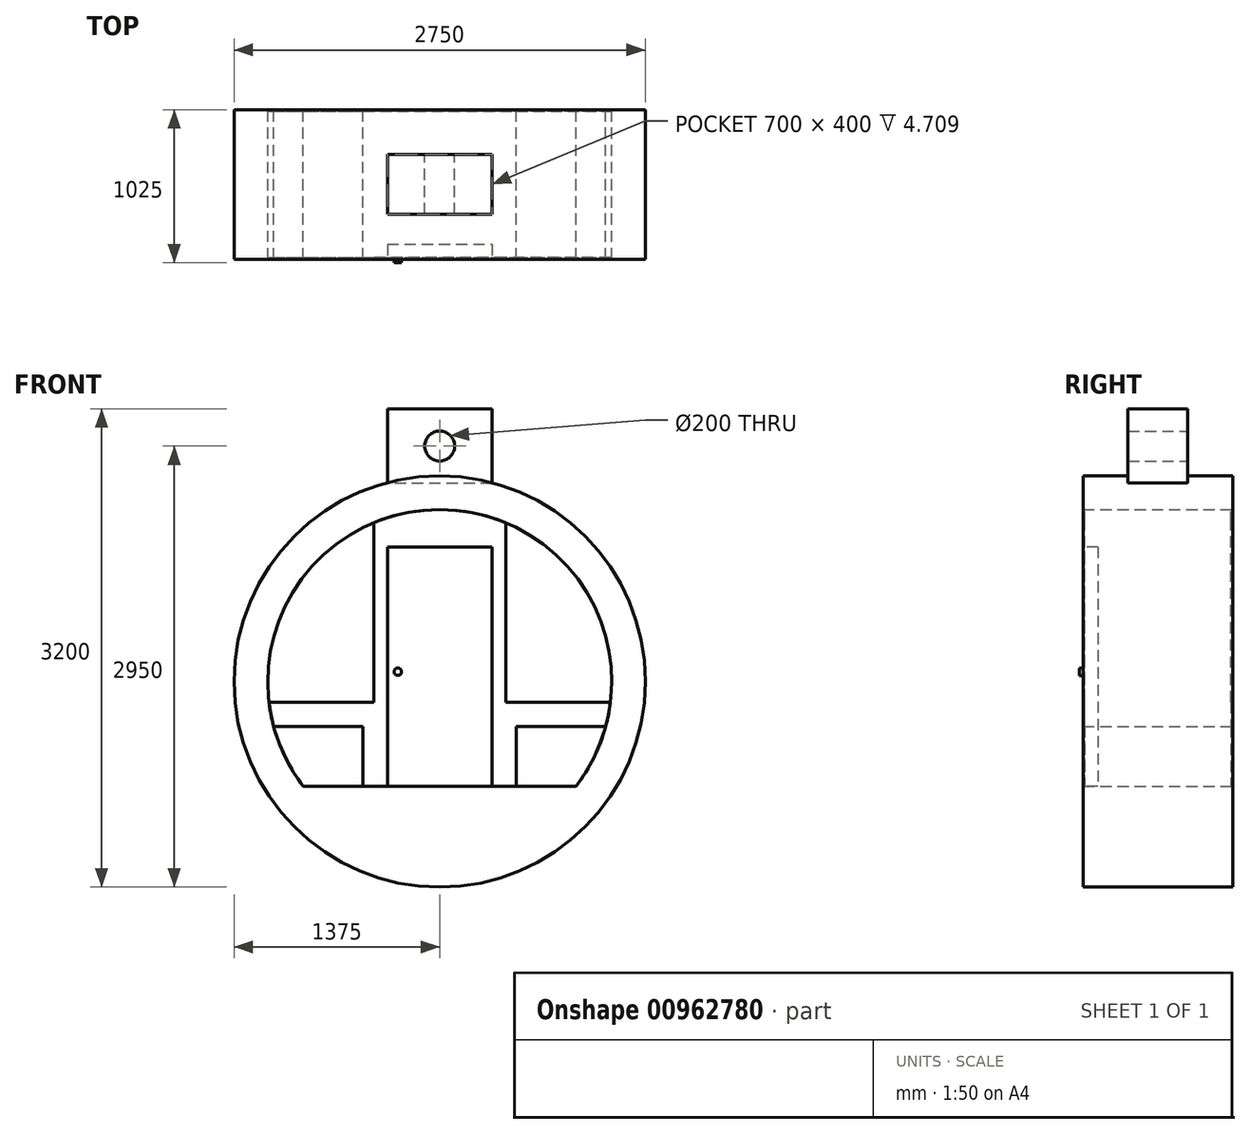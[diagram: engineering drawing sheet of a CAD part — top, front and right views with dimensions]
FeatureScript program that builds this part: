
annotation { "Feature Type Name" : "Feature", "Feature Type Description" : "" }
export const myFeature = defineFeature(function(context is Context, id is Id, definition is map)
    precondition{}
    {
        {
            var Q0;
            Q0=qCreatedBy(makeId("Front.planeOp"),FACE);
            var sketch = newSketch(context, id + "F0", { "sketchPlane" : qUnion([Q0])});
            skLineSegment(sketch, "E0.bottom", {"start": v(350, 3250) * mm, "end": v(-350, 3250) * mm});
            skLineSegment(sketch, "E0.top", {"start": v(350, 2750) * mm, "end": v(-350, 2750) * mm});
            skLineSegment(sketch, "E0.left", {"start": v(350, 3250) * mm, "end": v(350, 2750) * mm});
            skLineSegment(sketch, "E0.right", {"start": v(-350, 3250) * mm, "end": v(-350, 2750) * mm});
            skPoint(sketch, "E0.middle", {"position": v(0, 3000) * mm});
            skCircle(sketch, "E1", {"center": v(0, 3000) * mm, "radius": 100 * mm});
            skSolve(sketch);
        }
        {
            var Q0;
            Q0=qSketchRegion(id+"F0",true);
            extrude(context, id + "F1", {"entities" : qUnion([Q0]), "endBound" : BoundingType.SYMMETRIC, "depth" : 400 * mm, "offsetDistance" : 25 * mm});
        }
        {
            var Q0;
            Q0=qCreatedBy(makeId("Front.planeOp"),FACE);
            var sketch = newSketch(context, id + "F2", { "sketchPlane" : qUnion([Q0])});
            skLineSegment(sketch, "E2", {"start": v(0, 0) * mm, "end": v(0, 2750) * mm, "construction": true});
            skPoint(sketch, "E3", {"position": v(0, 1375) * mm});
            skCircle(sketch, "E4", {"center": v(0, 1375) * mm, "radius": 1375 * mm});
            skCircle(sketch, "E5", {"center": v(0, 1375) * mm, "radius": 1150 * mm});
            skLineSegment(sketch, "E6", {"start": v(-912.41, 675) * mm, "end": v(912.41, 675) * mm});
            skSolve(sketch);
        }
        {
            var Q0;
            Q0=qSketchRegion(id+"F2",true);
            var Q1;
            {var subQ0=sQuery(id+"F2.wireOp",EDGE,"E6");Q1=makeQuery(id+"F2.imprint","IMPRINT",FACE,{"disambiguationData":[TD([[makeQuery(id+"F2.imprint","IMPRINT",EDGE,{"derivedFrom":subQ0}),-1.0]])]});}
            extrude(context, id + "F3", {"entities" : qUnion([Q0, Q1]), "operationType" : NewBodyOperationType.ADD, "endBound" : BoundingType.SYMMETRIC, "depth" : 1000 * mm, "offsetDistance" : 25 * mm});
        }
        {
            var Q0;
            Q0=qCreatedBy(makeId("Front.planeOp"),FACE);
            var sketch = newSketch(context, id + "F4", { "sketchPlane" : qUnion([Q0])});
            skLineSegment(sketch, "E7", {"start": v(512.41, 675) * mm, "end": v(512.41, 1075) * mm});
            skLineSegment(sketch, "E8", {"start": v(512.41, 1075) * mm, "end": v(1110.18, 1075) * mm});
            skLineSegment(sketch, "E9.MirrorCS", {"start": v(-512.41, 675) * mm, "end": v(-512.41, 1075) * mm});
            skLineSegment(sketch, "E10.MirrorCS", {"start": v(-512.41, 1075) * mm, "end": v(-1110.18, 1075) * mm});
            skLineSegment(sketch, "E11", {"start": v(512.41, 675) * mm, "end": v(912.41, 675) * mm});
            skArc(sketch, "E12", {"start": v(912.41, 675) * mm, "mid": v(1030.88, 865.32) * mm, "end": v(1110.18, 1075) * mm});
            skArc(sketch, "E13.MirrorCS", {"start": v(-912.41, 675) * mm, "mid": v(-1030.88, 865.32) * mm, "end": v(-1110.18, 1075) * mm});
            skLineSegment(sketch, "E14.MirrorCS", {"start": v(-512.41, 675) * mm, "end": v(-912.41, 675) * mm});
            skSolve(sketch);
        }
        {
            var Q0;
            Q0=qSketchRegion(id+"F4",true);
            extrude(context, id + "F5", {"entities" : qUnion([Q0]), "endBound" : BoundingType.SYMMETRIC, "depth" : 1000 * mm, "offsetDistance" : 25 * mm});
        }
        {
            var Q0;
            Q0=makeQuery(id+"F3.opExtrude","CAP_FACE",FACE,{"disambiguationData":[OSD([sQuery(id+"F2.wireOp",EDGE,"E4"),sQuery(id+"F2.wireOp",EDGE,"E5"),sQuery(id+"F2.wireOp",EDGE,"E6")])],"isStart":false});
            var sketch = newSketch(context, id + "F6", { "sketchPlane" : qUnion([Q0])});
            skLineSegment(sketch, "E15", {"start": v(-350, 2275) * mm, "end": v(350, 2275) * mm});
            skLineSegment(sketch, "E16", {"start": v(350, 2275) * mm, "end": v(350, 675) * mm});
            skLineSegment(sketch, "E17", {"start": v(350, 675) * mm, "end": v(-350, 675) * mm});
            skLineSegment(sketch, "E18", {"start": v(-350, 675) * mm, "end": v(-350, 2275) * mm});
            skPoint(sketch, "E19", {"position": v(0, 675) * mm});
            skSolve(sketch);
        }
        {
            var Q0;
            Q0=qSketchRegion(id+"F6",true);
            extrude(context, id + "F7", {"entities" : qUnion([Q0]), "oppositeDirection" : true, "depth" : 100 * mm, "offsetDistance" : 25 * mm});
        }
        {
            var Q0;
            Q0=makeQuery(id+"F7.opExtrude","CAP_FACE",FACE,{"disambiguationData":[OSD([sQuery(id+"F6.wireOp",EDGE,"E15"),sQuery(id+"F6.wireOp",EDGE,"E16"),sQuery(id+"F6.wireOp",EDGE,"E17"),sQuery(id+"F6.wireOp",EDGE,"E18")])],"isStart":true});
            var sketch = newSketch(context, id + "F8", { "sketchPlane" : qUnion([Q0])});
            skCircle(sketch, "E20", {"center": v(-280, 1440.53) * mm, "radius": 25 * mm});
            skSolve(sketch);
        }
        {
            var Q0;
            Q0=qSketchRegion(id+"F8",true);
            extrude(context, id + "F9", {"entities" : qUnion([Q0]), "depth" : 25 * mm, "offsetDistance" : 25 * mm});
        }
        {
            var Q0;
            Q0=makeQuery(id+"F7.opExtrude","CAP_FACE",FACE,{"disambiguationData":[OSD([sQuery(id+"F6.wireOp",EDGE,"E15"),sQuery(id+"F6.wireOp",EDGE,"E16"),sQuery(id+"F6.wireOp",EDGE,"E17"),sQuery(id+"F6.wireOp",EDGE,"E18")])],"isStart":true});
            var sketch = newSketch(context, id + "F10", { "sketchPlane" : qUnion([Q0])});
            skLineSegment(sketch, "E21", {"start": v(-1141.67, 1236.8) * mm, "end": v(-441.67, 1236.8) * mm});
            skLineSegment(sketch, "E22", {"start": v(-441.67, 1236.8) * mm, "end": v(-441.67, 2436.8) * mm});
            skArc(sketch, "E23", {"start": v(-441.67, 2436.8) * mm, "mid": v(0, 2525) * mm, "end": v(441.67, 2436.8) * mm});
            skArc(sketch, "E24", {"start": v(-1141.67, 1236.8) * mm, "mid": v(-1128.83, 1155.34) * mm, "end": v(-1110.18, 1075) * mm});
            skLineSegment(sketch, "E25.MirrorCS", {"start": v(441.67, 1236.8) * mm, "end": v(441.67, 2436.8) * mm});
            skLineSegment(sketch, "E26.MirrorCS", {"start": v(1141.67, 1236.8) * mm, "end": v(441.67, 1236.8) * mm});
            skArc(sketch, "E27.MirrorCS", {"start": v(1141.67, 1236.8) * mm, "mid": v(1128.83, 1155.34) * mm, "end": v(1110.18, 1075) * mm});
            skLineSegment(sketch, "E28", {"start": v(-1110.18, 1075) * mm, "end": v(-512.41, 1075) * mm});
            skLineSegment(sketch, "E29", {"start": v(-512.41, 1075) * mm, "end": v(-512.41, 675) * mm});
            skLineSegment(sketch, "E30", {"start": v(-512.41, 675) * mm, "end": v(-350, 675) * mm});
            skLineSegment(sketch, "E31", {"start": v(-350, 675) * mm, "end": v(-350, 2275) * mm});
            skLineSegment(sketch, "E32", {"start": v(-350, 2275) * mm, "end": v(350, 2275) * mm});
            skLineSegment(sketch, "E33", {"start": v(350, 2275) * mm, "end": v(350, 675) * mm});
            skLineSegment(sketch, "E34", {"start": v(350, 675) * mm, "end": v(512.41, 675) * mm});
            skLineSegment(sketch, "E35", {"start": v(512.41, 675) * mm, "end": v(512.41, 1075) * mm});
            skLineSegment(sketch, "E36", {"start": v(512.41, 1075) * mm, "end": v(1110.18, 1075) * mm});
            skSolve(sketch);
        }
        {
            var Q0;
            Q0=qSketchRegion(id+"F10",true);
            extrude(context, id + "F11", {"entities" : qUnion([Q0]), "oppositeDirection" : true, "depth" : 10 * mm, "offsetDistance" : 25 * mm});
        }
        {
            var Q0;
            Q0=makeQuery(id+"F11.opExtrude","SWEPT_BODY",BODY,{"disambiguationData":[OSD([sQuery(id+"F10.wireOp",EDGE,"E21"),sQuery(id+"F10.wireOp",EDGE,"E22"),sQuery(id+"F10.wireOp",EDGE,"E23"),sQuery(id+"F10.wireOp",EDGE,"E24"),sQuery(id+"F10.wireOp",EDGE,"E25.MirrorCS"),sQuery(id+"F10.wireOp",EDGE,"E26.MirrorCS"),sQuery(id+"F10.wireOp",EDGE,"E27.MirrorCS"),sQuery(id+"F10.wireOp",EDGE,"E28"),sQuery(id+"F10.wireOp",EDGE,"E29"),sQuery(id+"F10.wireOp",EDGE,"E30"),sQuery(id+"F10.wireOp",EDGE,"E31"),sQuery(id+"F10.wireOp",EDGE,"E32"),sQuery(id+"F10.wireOp",EDGE,"E33"),sQuery(id+"F10.wireOp",EDGE,"E34"),sQuery(id+"F10.wireOp",EDGE,"E35"),sQuery(id+"F10.wireOp",EDGE,"E36")])]});
            var Q1;
            Q1=qCreatedBy(makeId("Front.planeOp"),FACE);
            mirror(context, id + "F12", {"entities" : qUnion([Q0]), "mirrorPlane" : qUnion([Q1])});
        }
        {
            var Q0;
            Q0=makeQuery(id+"F12.opPattern","COPY",FACE,{"derivedFrom":makeQuery(id+"F11.opExtrude","CAP_FACE",FACE,{"disambiguationData":[OSD([sQuery(id+"F10.wireOp",EDGE,"E21"),sQuery(id+"F10.wireOp",EDGE,"E22"),sQuery(id+"F10.wireOp",EDGE,"E23"),sQuery(id+"F10.wireOp",EDGE,"E24"),sQuery(id+"F10.wireOp",EDGE,"E25.MirrorCS"),sQuery(id+"F10.wireOp",EDGE,"E26.MirrorCS"),sQuery(id+"F10.wireOp",EDGE,"E27.MirrorCS"),sQuery(id+"F10.wireOp",EDGE,"E28"),sQuery(id+"F10.wireOp",EDGE,"E29"),sQuery(id+"F10.wireOp",EDGE,"E30"),sQuery(id+"F10.wireOp",EDGE,"E31"),sQuery(id+"F10.wireOp",EDGE,"E32"),sQuery(id+"F10.wireOp",EDGE,"E33"),sQuery(id+"F10.wireOp",EDGE,"E34"),sQuery(id+"F10.wireOp",EDGE,"E35"),sQuery(id+"F10.wireOp",EDGE,"E36")])],"isStart":true}),"instanceName":"1"});
            var sketch = newSketch(context, id + "F13", { "sketchPlane" : qUnion([Q0])});
            skLineSegment(sketch, "E37.bottom", {"start": v(-350, 2275) * mm, "end": v(350, 2275) * mm});
            skLineSegment(sketch, "E37.top", {"start": v(-350, 675) * mm, "end": v(350, 675) * mm});
            skLineSegment(sketch, "E37.left", {"start": v(-350, 2275) * mm, "end": v(-350, 675) * mm});
            skLineSegment(sketch, "E37.right", {"start": v(350, 2275) * mm, "end": v(350, 675) * mm});
            skSolve(sketch);
        }
        {
            var Q0;
            Q0=qSketchRegion(id+"F13",true);
            extrude(context, id + "F14", {"entities" : qUnion([Q0]), "operationType" : NewBodyOperationType.ADD, "oppositeDirection" : true, "depth" : 10 * mm, "offsetDistance" : 25 * mm});
        }
        {
            var Q0;
            Q0=makeQuery(id+"F1.opExtrude","SWEPT_BODY",BODY,{"disambiguationData":[OSD([sQuery(id+"F0.wireOp",EDGE,"E0.bottom"),sQuery(id+"F0.wireOp",EDGE,"E0.top"),sQuery(id+"F0.wireOp",EDGE,"E0.left"),sQuery(id+"F0.wireOp",EDGE,"E0.right"),sQuery(id+"F0.wireOp",EDGE,"E1")])]});
            transform(context, id + "F15", {"entities" : qUnion([Q0]), "transformType" : TransformType.TRANSLATION_3D, "dx" : 0 * mm, "dy" : 0 * mm, "dz" : -50 * mm, "makeCopy" : false});
        }
        {
            var Q0;
            Q0=makeQuery(id+"F1.opExtrude","SWEPT_BODY",BODY,{"disambiguationData":[OSD([sQuery(id+"F0.wireOp",EDGE,"E0.bottom"),sQuery(id+"F0.wireOp",EDGE,"E0.top"),sQuery(id+"F0.wireOp",EDGE,"E0.left"),sQuery(id+"F0.wireOp",EDGE,"E0.right"),sQuery(id+"F0.wireOp",EDGE,"E1")])]});
            var Q1;
            Q1=makeQuery(id+"F3.opExtrude","SWEPT_BODY",BODY,{"disambiguationData":[OSD([sQuery(id+"F2.wireOp",EDGE,"E4"),sQuery(id+"F2.wireOp",EDGE,"E5"),sQuery(id+"F2.wireOp",EDGE,"E6")])]});
            booleanBodies(context, id + "F16", {"operationType" : BooleanOperationType.SUBTRACTION, "tools" : qUnion([Q0]), "targets" : qUnion([Q1]), "keepTools" : true});
        }
    });
